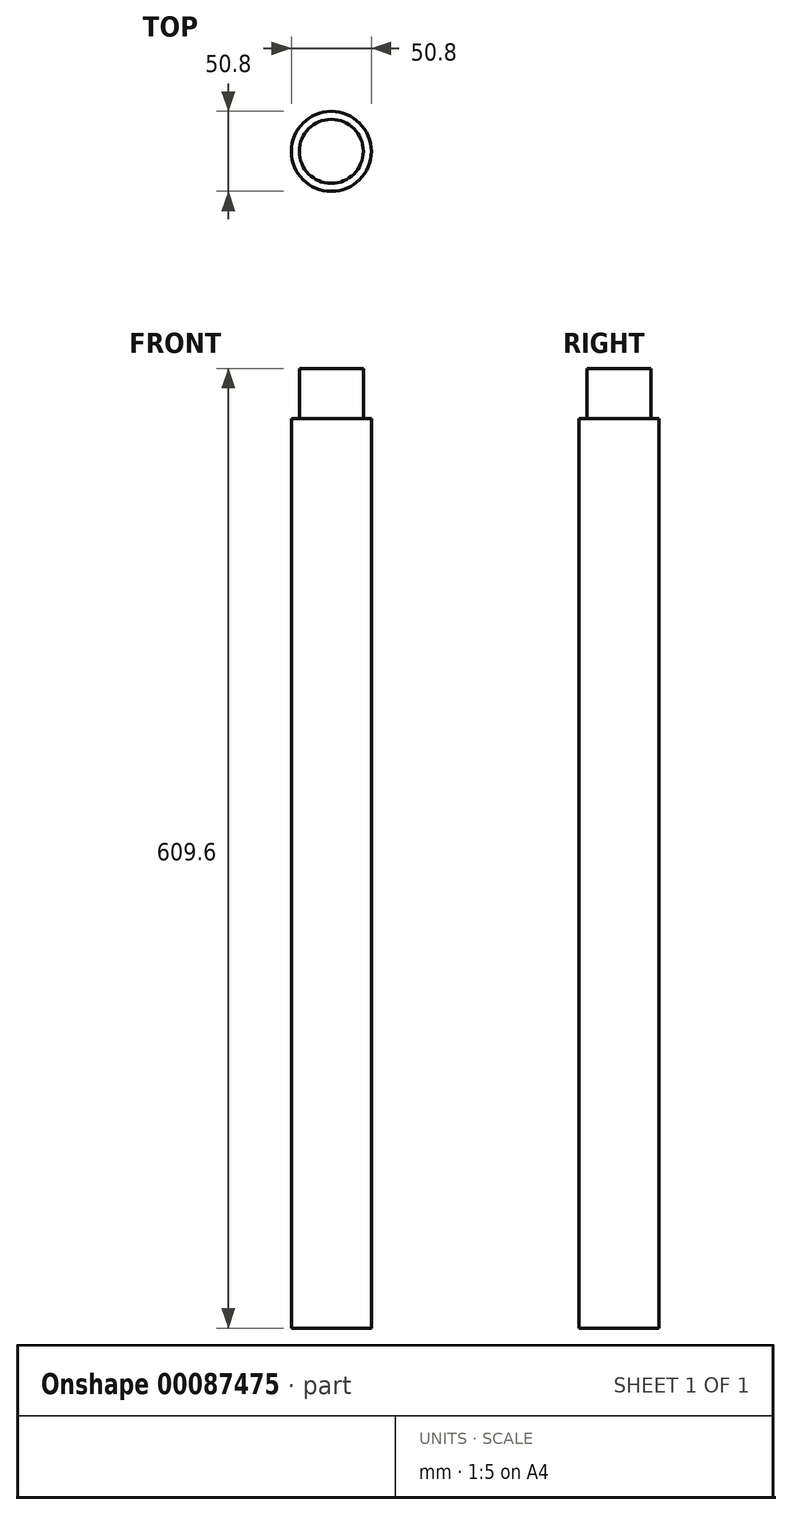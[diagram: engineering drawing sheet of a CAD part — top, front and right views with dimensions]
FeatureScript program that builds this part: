
annotation { "Feature Type Name" : "Feature", "Feature Type Description" : "" }
export const myFeature = defineFeature(function(context is Context, id is Id, definition is map)
    precondition{}
    {
        {
            var Q0;
            Q0=qCreatedBy(makeId("Top.planeOp"),FACE);
            var sketch = newSketch(context, id + "F0", { "sketchPlane" : qUnion([Q0])});
            skCircle(sketch, "E0", {"center": v(0, 0) * mm, "radius": 25.4 * mm});
            skCircle(sketch, "E1", {"center": v(0, 0) * mm, "radius": 19.05 * mm, "construction": true});
            skSolve(sketch);
        }
        {
            var Q0;
            Q0=makeQuery(id+"F0.imprint","IMPRINT",FACE,{"disambiguationData":[TD([[makeQuery(id+"F0.imprint","IMPRINT",EDGE,{"derivedFrom":sQuery(id+"F0.wireOp",EDGE,"E0")}),1.0]])]});
            extrude(context, id + "F1", {"entities" : qUnion([Q0]), "depth" : 609.6 * mm});
        }
        {
            var Q0;
            Q0=makeQuery(id+"F1.opExtrude","CAP_FACE",FACE,{"disambiguationData":[OSD([sQuery(id+"F0.wireOp",EDGE,"E0")])],"isStart":false});
            var sketch = newSketch(context, id + "F2", { "sketchPlane" : qUnion([Q0])});
            skCircle(sketch, "E2", {"center": v(0, 0) * mm, "radius": 20.32 * mm});
            skCircle(sketch, "E3.0", {"center": v(0, 0) * mm, "radius": 25.4 * mm});
            skSolve(sketch);
        }
        {
            var Q0;
            Q0 = qSketchRegion(id + "F2", true);
            extrude(context, id + "F3", {"entities" : qUnion([Q0]), "operationType" : NewBodyOperationType.REMOVE, "oppositeDirection" : true, "depth" : 31.75 * mm});
        }
    });
